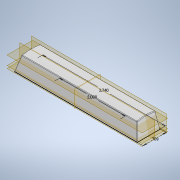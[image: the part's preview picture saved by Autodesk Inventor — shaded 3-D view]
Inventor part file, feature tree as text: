
AUTODESK INVENTOR PART (.ipt)
format: ipt  version: 2022 (Build 260153000, 153)  size: 386,560 bytes
history: native  units: in
note: dims shown in document units (in); Inventor stores cm internally (conversion verified against a paired STEP export)
features: sketch x8, extrude x7, other x4, projected_geometry x3, fillet x2, mirror x1, shell x1
ambient origin geometry x8: Origin, YZ Plane, XZ Plane, XY Plane, X Axis, Y Axis, Z Axis, Center Point
bodies: Body1 (feature_tree)
feature tree (26):
  other  "ソリッド1"
  sketch  "スケッチ1"
  extrude  "押し出し1"  Depth=0.7087in
  extrude  "押し出し2"  Depth=3.7402in
  other  "作業平面1"
  extrude  "押し出し3"  Depth=2.0in
  mirror  "ミラー1"
  sketch  "スケッチ7"
  shell  "シェル1"  Thickness=0.463in
  extrude  "押し出し4"  Depth=0.5841in
  other  "作業平面2"
  extrude  "押し出し5"  Depth=0.5209in
  fillet  "フィレット2"  Radius=0.4331in
  other  "作業平面3"
  extrude  "押し出し6"  TaperAngle=0.0deg  [1 undecoded]
  extrude  "押し出し7"  Depth=0.5202in
  fillet  "フィレット3"  Radius=1.0in
  sketch  "スケッチ2"
  sketch  "スケッチ3"
  sketch  "スケッチ5"
  sketch  "スケッチ8"
  sketch  "スケッチ9"
  sketch  "スケッチ10"
  projected_geometry  "投影ループ1"
  projected_geometry  "投影ループ2"
  projected_geometry  "投影ループ3"
note: 1 required parameter value undecoded (feature->parameter linkage not recoverable at this tier; creation-order binding heuristic only, values carry confidence <= 0.55)
